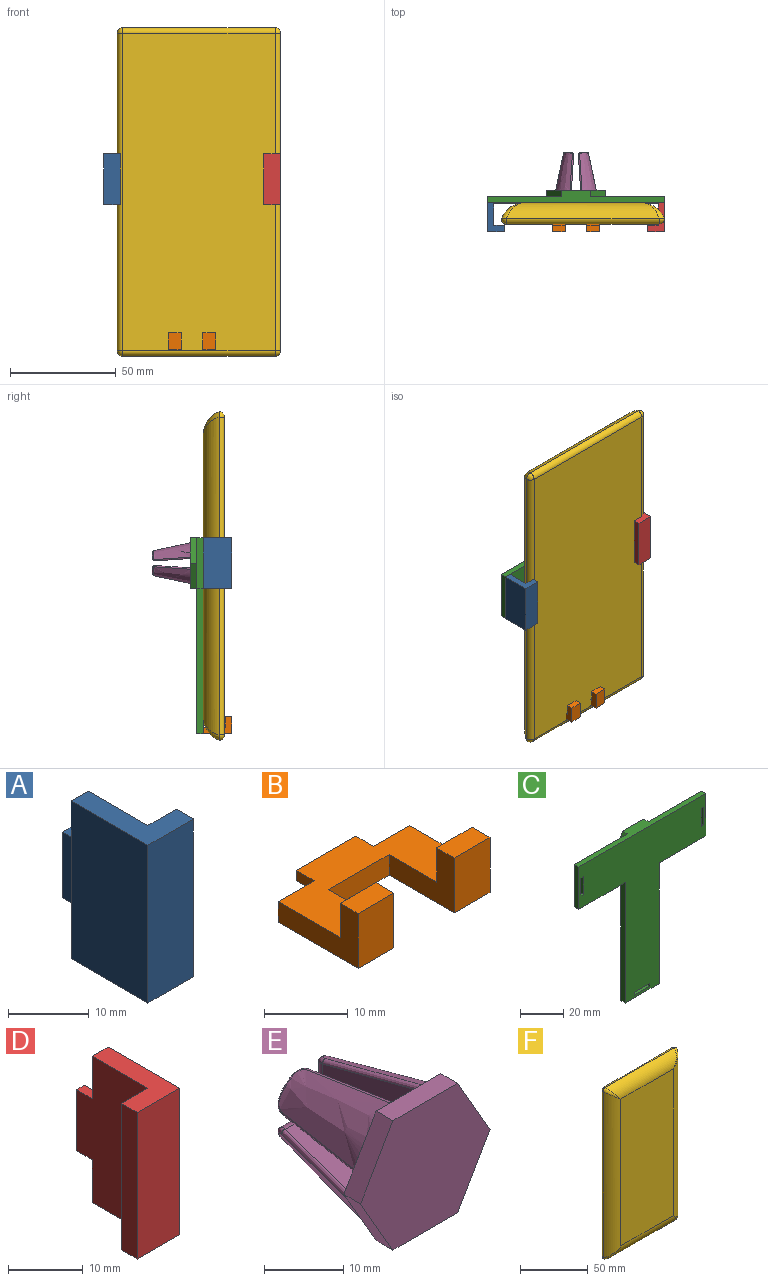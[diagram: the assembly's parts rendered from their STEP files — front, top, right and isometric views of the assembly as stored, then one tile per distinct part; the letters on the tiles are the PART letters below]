
ASSEMBLY  parts=6 mates=5
PART A: 12 faces, bbox 8x16.5x24 mm
  f0: plane 13.5x8mm, normal (0,0,-1), area 55.5mm2, adj f1,f4,f5,f6,f7,f11
  f1: plane 24x13.5mm, normal (1,0,0), area 282mm2, adj f0,f2,f3,f7,f8,f10,f11
  f2: plane 13.5x8mm, normal (0,0,1), area 55.5mm2, adj f1,f4,f5,f6,f7,f11
  f3: plane 10x1.5mm, normal (0,1,0), area 15mm2, adj f1,f8,f9,f10
  f4: plane 24x13.5mm, normal (-1,0,0), area 324mm2, adj f0,f2,f6,f11
  f5: plane 24x3mm, normal (1,0,0), area 72mm2, adj f0,f2,f6,f7
  f6: plane 24x8mm, normal (0,-1,0), area 192mm2, adj f0,f2,f4,f5
  f7: plane 24x5mm, normal (0,1,0), area 120mm2, adj f0,f1,f2,f5
  f8: plane 3x1.5mm, normal (0,0,1), area 4.5mm2, adj f1,f3,f9,f11
  f9: plane 10x3mm, normal (-1,0,0), area 30mm2, adj f3,f8,f10,f11
  f10: plane 3x1.5mm, normal (0,0,-1), area 4.5mm2, adj f1,f3,f9,f11
  f11: plane 24x3mm, normal (0,1,0), area 57mm2, adj f0,f1,f2,f4,f8,f9,f10
PART B: 18 faces, bbox 22.2x16.5x8 mm
  f0: plane 10x1.5mm, normal (0,1,0), area 15mm2, adj f1,f2,f3,f4
  f1: plane 22.2x13.5mm, normal (0,0,1), area 181.5mm2, adj f0,f3,f4,f5,f6,f7,f9,f12
  f2: plane 10x3mm, normal (0,0,-1), area 30mm2, adj f0,f3,f4,f5
  f3: plane 3x1.5mm, normal (-1,0,0), area 4.5mm2, adj f0,f1,f2,f5
  f4: plane 3x1.5mm, normal (1,0,0), area 4.5mm2, adj f0,f1,f2,f5
  f5: plane 22.2x3mm, normal (0,1,0), area 51.6mm2, adj f1,f2,f3,f4,f7,f8,f16
  f6: plane 11x8mm, normal (1,0,0), area 48mm2, adj f1,f8,f9,f10,f11,f17
  f7: plane 13.5x8mm, normal (-1,0,0), area 55.5mm2, adj f1,f5,f8,f9,f10,f11
  f8: plane 22.2x13.5mm, normal (0,0,-1), area 187.5mm2, adj f5,f6,f7,f11,f12,f15,f16,f17
  f9: plane 6x5mm, normal (0,1,0), area 30mm2, adj f1,f6,f7,f10
  f10: plane 6x3mm, normal (0,0,1), area 18mm2, adj f6,f7,f9,f11
  f11: plane 8x6mm, normal (0,-1,0), area 48mm2, adj f6,f7,f8,f10
  f12: plane 11x8mm, normal (-1,0,0), area 48mm2, adj f1,f8,f13,f14,f15,f17
  f13: plane 6x5mm, normal (0,1,0), area 30mm2, adj f1,f12,f14,f16
  f14: plane 6x3mm, normal (0,0,1), area 18mm2, adj f12,f13,f15,f16
  f15: plane 8x6mm, normal (0,-1,0), area 48mm2, adj f8,f12,f14,f16
  f16: plane 13.5x8mm, normal (1,0,0), area 55.5mm2, adj f1,f5,f8,f13,f14,f15
  f17: plane 10.2x3mm, normal (0,-1,0), area 30.6mm2, adj f1,f6,f8,f12
PART C: 35 faces, bbox 83.5x6x92.5 mm
  f0: plane 68.5x3mm, normal (-1,0,0), area 205.5mm2, adj f2,f3,f4,f5
  f1: plane 68.5x3mm, normal (1,0,0), area 205.5mm2, adj f2,f3,f4,f9
  f2: plane 22.2x3mm, normal (0,0,-1), area 66.6mm2, adj f0,f1,f3,f4
  f3: plane 92.5x83.5mm, normal (0,1,0), area 2977.4mm2, adj f0,f1,f2,f5,f6,f7,f8,f9
  f4: plane 92.5x83.5mm, normal (0,-1,0), area 3476.2mm2, adj f0,f1,f2,f5,f6,f7,f8,f9
  f5: plane 30.65x3mm, normal (0,0,-1), area 91.9mm2, adj f0,f3,f4,f8
  f6: plane 24x3mm, normal (1,0,0), area 72mm2, adj f3,f4,f7,f9
  f7: plane 83.5x6mm, normal (0,0,1), area 292.1mm2, adj f3,f4,f6,f8,f16,f17,f21
  f8: plane 24x3mm, normal (-1,0,0), area 72mm2, adj f3,f4,f5,f7
  f9: plane 30.65x3mm, normal (0,0,-1), area 91.9mm2, adj f1,f3,f4,f6
  f10: plane 10.1x5.83mm, normal (0.87,0,-0.5), area 35mm2, adj f11,f20,f21,f22
  f11: plane 10.1x5.83mm, normal (0.87,0,0.5), area 35mm2, adj f10,f12,f21,f22
  f12: plane 11.66x3mm, normal (0,0,1), area 35mm2, adj f11,f13,f21,f22
  f13: plane 10.1x5.83mm, normal (-0.87,0,0.5), area 35mm2, adj f12,f14,f21,f22
  f14: plane 10.1x5.83mm, normal (-0.87,0,-0.5), area 35mm2, adj f13,f20,f21,f22
  f15: plane 12x6.93mm, normal (-0.87,0,-0.5), area 41.6mm2, adj f3,f16,f19,f21
  f16: plane 12x6.93mm, normal (-0.87,0,0.5), area 41.6mm2, adj f3,f7,f15,f21
  f17: plane 12x6.93mm, normal (0.87,0,0.5), area 41.6mm2, adj f3,f7,f18,f21
  f18: plane 12x6.93mm, normal (0.87,0,-0.5), area 41.6mm2, adj f3,f17,f19,f21
  f19: plane 13.86x3mm, normal (0,0,-1), area 41.6mm2, adj f3,f15,f18,f21
  f20: plane 11.66x3mm, normal (0,0,-1), area 35mm2, adj f10,f14,f21,f22
  f21: plane 27.71x24mm, normal (0,1,0), area 145.5mm2, adj f7,f10,f11,f12,f13,f14,f15,f16
  f22: plane 23.33x20.2mm, normal (0,1,0), area 353.4mm2, adj f10,f11,f12,f13,f14,f20
  f23: plane 10.1x3mm, normal (1,0,0), area 30.3mm2, adj f3,f4,f24,f25
  f24: plane 3x1.6mm, normal (0,0,-1), area 4.8mm2, adj f3,f4,f23,f26
  f25: plane 3x1.6mm, normal (0,0,1), area 4.8mm2, adj f3,f4,f23,f26
  f26: plane 10.1x3mm, normal (-1,0,0), area 30.3mm2, adj f3,f4,f24,f25
  f27: plane 10.1x3mm, normal (0,0,1), area 30.3mm2, adj f3,f4,f28,f29
  f28: plane 3x1.6mm, normal (1,0,0), area 4.8mm2, adj f3,f4,f27,f30
  f29: plane 3x1.6mm, normal (-1,0,0), area 4.8mm2, adj f3,f4,f27,f30
  f30: plane 10.1x3mm, normal (0,0,-1), area 30.3mm2, adj f3,f4,f28,f29
  f31: plane 10.1x3mm, normal (1,0,0), area 30.3mm2, adj f3,f4,f32,f33
  f32: plane 3x1.6mm, normal (0,0,-1), area 4.8mm2, adj f3,f4,f31,f34
  f33: plane 3x1.6mm, normal (0,0,1), area 4.8mm2, adj f3,f4,f31,f34
  f34: plane 10.1x3mm, normal (-1,0,0), area 30.3mm2, adj f3,f4,f32,f33
PART D: 12 faces, bbox 8x16.5x24 mm
  f0: plane 13.5x8mm, normal (0,0,-1), area 55.5mm2, adj f1,f3,f5,f6,f7,f11
  f1: plane 24x13.5mm, normal (1,0,0), area 324mm2, adj f0,f4,f6,f11
  f2: plane 10x1.5mm, normal (0,1,0), area 15mm2, adj f3,f8,f9,f10
  f3: plane 24x13.5mm, normal (-1,0,0), area 282mm2, adj f0,f2,f4,f7,f8,f10,f11
  f4: plane 13.5x8mm, normal (0,0,1), area 55.5mm2, adj f1,f3,f5,f6,f7,f11
  f5: plane 24x3mm, normal (-1,0,0), area 72mm2, adj f0,f4,f6,f7
  f6: plane 24x8mm, normal (0,-1,0), area 192mm2, adj f0,f1,f4,f5
  f7: plane 24x5mm, normal (0,1,0), area 120mm2, adj f0,f3,f4,f5
  f8: plane 3x1.5mm, normal (0,0,-1), area 4.5mm2, adj f2,f3,f9,f11
  f9: plane 10x3mm, normal (1,0,0), area 30mm2, adj f2,f8,f10,f11
  f10: plane 3x1.5mm, normal (0,0,1), area 4.5mm2, adj f2,f3,f9,f11
  f11: plane 24x3mm, normal (0,1,0), area 57mm2, adj f0,f1,f3,f4,f8,f9,f10
PART E: 60 faces, bbox 23.2x23.4x20.6 mm
  f0: bspline ~17.61x8.12mm, area 143.4mm2, adj f4,f18,f19,f20,f48,f52
  f1: bspline ~17.61x8.12mm, area 143.4mm2, adj f4,f22,f23,f24,f43,f47
  f2: bspline ~17.61x8.12mm, area 143.4mm2, adj f4,f26,f27,f28,f38,f42
  f3: bspline ~17.61x8.12mm, area 143.4mm2, adj f4,f30,f31,f32,f33,f37
  f4: plane 23.15x20.06mm, normal (0,1,0), area 188.5mm2, adj f0,f1,f2,f3,f6,f7,f9,f10
  f5: plane 2.36x2.36mm, normal (0,1,0), area 3.3mm2, adj f31,f34,f36
  f6: plane 16.4x7.48mm, normal (-1,-0.07,0), area 85.4mm2, adj f4,f29,f32,f34
  f7: plane 16.4x7.48mm, normal (0,-0.07,-1), area 85.4mm2, adj f4,f29,f30,f36
  f8: plane 2.36x2.36mm, normal (0,1,0), area 3.3mm2, adj f27,f39,f41
  f9: plane 16.4x7.48mm, normal (1,-0.07,0), area 85.4mm2, adj f4,f25,f28,f39
  f10: plane 16.4x7.48mm, normal (0,-0.07,-1), area 85.4mm2, adj f4,f25,f26,f41
  f11: plane 2.36x2.36mm, normal (0,1,0), area 3.3mm2, adj f23,f44,f46
  f12: plane 16.4x7.48mm, normal (-1,-0.07,0), area 85.4mm2, adj f4,f21,f24,f44
  f13: plane 16.4x7.48mm, normal (0,-0.07,1), area 85.4mm2, adj f4,f21,f22,f46
  f14: plane 2.36x2.36mm, normal (0,1,0), area 3.3mm2, adj f19,f49,f51
  f15: plane 16.4x7.48mm, normal (0,-0.07,1), area 85.4mm2, adj f4,f17,f20,f49
  f16: plane 16.4x7.48mm, normal (1,-0.07,0), area 85.4mm2, adj f4,f17,f18,f51
  f17: cylinder r=0.5mm len=16.41mm, axis (-0.07,-1,-0.07), area 12.9mm2, adj f4,f15,f16,f50
  f18: bspline ~22.72x5.45mm, area 15.7mm2, adj f0,f4,f16,f52
  f19: bspline ~3.89x3.54mm, area 2.4mm2, adj f0,f14,f48,f52
  f20: bspline ~22.72x5.45mm, area 15.7mm2, adj f0,f4,f15,f48
  f21: cylinder r=0.5mm len=16.41mm, axis (0.07,-1,-0.07), area 12.9mm2, adj f4,f12,f13,f45
  f22: bspline ~22.72x5.45mm, area 15.7mm2, adj f1,f4,f13,f47
  f23: bspline ~3.89x3.54mm, area 2.4mm2, adj f1,f11,f43,f47
  f24: bspline ~22.72x5.45mm, area 15.7mm2, adj f1,f4,f12,f43
  f25: cylinder r=0.5mm len=16.41mm, axis (-0.07,-1,0.07), area 12.9mm2, adj f4,f9,f10,f40
  f26: bspline ~22.72x5.45mm, area 15.7mm2, adj f2,f4,f10,f42
  f27: bspline ~3.89x3.54mm, area 2.4mm2, adj f2,f8,f38,f42
  f28: bspline ~22.72x5.45mm, area 15.7mm2, adj f2,f4,f9,f38
  f29: cylinder r=0.5mm len=16.41mm, axis (-0.07,1,-0.07), area 12.9mm2, adj f4,f6,f7,f35
  f30: bspline ~20.18x4.91mm, area 15.7mm2, adj f3,f4,f7,f37
  f31: bspline ~3.62x3.43mm, area 2.4mm2, adj f3,f5,f33,f37
  f32: bspline ~20.18x4.91mm, area 15.7mm2, adj f3,f4,f6,f33
  f33: bspline ~2.03x1.75mm, area 1.9mm2, adj f3,f31,f32,f34
  f34: cylinder r=1.5mm len=4mm, axis (0,0,-1), area 7.8mm2, adj f5,f6,f33,f35
  f35: bspline ~1.76x1.5mm, area 0.9mm2, adj f29,f34,f36
  f36: cylinder r=1.5mm len=4mm, axis (-1,0,0), area 7.8mm2, adj f5,f7,f35,f37
  f37: bspline ~1.99x1.93mm, area 1.9mm2, adj f3,f30,f31,f36
  f38: bspline ~1.99x1.93mm, area 1.9mm2, adj f2,f27,f28,f39
  f39: cylinder r=1.5mm len=4mm, axis (0,0,-1), area 7.8mm2, adj f8,f9,f38,f40
  f40: bspline ~1.76x1.5mm, area 0.9mm2, adj f25,f39,f41
  f41: cylinder r=1.5mm len=4mm, axis (1,0,0), area 7.8mm2, adj f8,f10,f40,f42
  f42: bspline ~2.03x1.75mm, area 1.9mm2, adj f2,f26,f27,f41
  f43: bspline ~1.99x1.93mm, area 1.9mm2, adj f1,f23,f24,f44
  f44: cylinder r=1.5mm len=4mm, axis (0,0,1), area 7.8mm2, adj f11,f12,f43,f45
  f45: bspline ~1.76x1.5mm, area 0.9mm2, adj f21,f44,f46
  f46: cylinder r=1.5mm len=4mm, axis (-1,0,0), area 7.8mm2, adj f11,f13,f45,f47
  f47: bspline ~2.03x1.75mm, area 1.9mm2, adj f1,f22,f23,f46
  f48: bspline ~1.99x1.93mm, area 1.9mm2, adj f0,f19,f20,f49
  f49: cylinder r=1.5mm len=4mm, axis (1,0,0), area 7.8mm2, adj f14,f15,f48,f50
  f50: bspline ~1.76x1.5mm, area 0.9mm2, adj f17,f49,f51
  f51: cylinder r=1.5mm len=4mm, axis (0,0,1), area 7.8mm2, adj f14,f16,f50,f52
  f52: bspline ~2.03x1.75mm, area 1.9mm2, adj f0,f18,f19,f51
  f53: plane 11.55x3mm, normal (0,0,1), area 34.6mm2, adj f4,f54,f58,f59
  f54: plane 10x5.77mm, normal (0.87,0,0.5), area 34.6mm2, adj f4,f53,f55,f59
  f55: plane 10x5.77mm, normal (0.87,0,-0.5), area 34.6mm2, adj f4,f54,f56,f59
  f56: plane 11.55x3mm, normal (0,0,-1), area 34.6mm2, adj f4,f55,f57,f59
  f57: plane 10x5.77mm, normal (-0.87,0,-0.5), area 34.6mm2, adj f4,f56,f58,f59
  f58: plane 10x5.77mm, normal (-0.87,0,0.5), area 34.6mm2, adj f4,f53,f57,f59
  f59: plane 23.09x20mm, normal (0,-1,0), area 346.4mm2, adj f53,f54,f55,f56,f57,f58
PART F: 18 faces, bbox 77x10x155 mm
  f0: plane 132.75x54.75mm, normal (0,-1,0), area 7268.3mm2, adj f10,f13,f14,f17
  f1: plane 150x72mm, normal (0,1,0), area 10800mm2, adj f3,f4,f7,f8
  f2: sphere r=2.5mm, area 9.8mm2, adj f3,f4,f11
  f3: cylinder r=2.5mm len=72mm, axis (-1,0,0), area 282.7mm2, adj f1,f2,f5,f13
  f4: cylinder r=2.5mm len=150mm, axis (0,0,-1), area 589mm2, adj f1,f2,f6,f10
  f5: sphere r=2.5mm, area 13.4mm2, adj f3,f7,f15
  f6: sphere r=2.5mm, area 9.8mm2, adj f4,f8,f12
  f7: cylinder r=2.5mm len=150mm, axis (0,0,1), area 589mm2, adj f1,f5,f9,f17
  f8: cylinder r=2.5mm len=72mm, axis (1,0,0), area 282.7mm2, adj f1,f6,f9,f14
  f9: sphere r=2.5mm, area 6.2mm2, adj f7,f8,f16
  f10: cylinder r=12mm len=150mm, axis (0,0,-1), area 2012.7mm2, adj f0,f4,f11,f12
  f11: bspline ~11.12x11.12mm, area 22.9mm2, adj f2,f10,f13
  f12: bspline ~11.12x11.12mm, area 22.9mm2, adj f6,f10,f14
  f13: cylinder r=12mm len=72mm, axis (1,0,0), area 902.3mm2, adj f0,f3,f11,f15
  f14: cylinder r=12mm len=72mm, axis (1,0,0), area 902.3mm2, adj f0,f8,f12,f16
  f15: bspline ~11.12x11.12mm, area 23.1mm2, adj f5,f13,f17
  f16: bspline ~11.12x11.12mm, area 22.9mm2, adj f9,f14,f17
  f17: cylinder r=12mm len=150mm, axis (0,0,-1), area 2012.7mm2, adj f0,f7,f15,f16
PLACE A t=(-81.2,-40.39,27.55)mm
PLACE B t=(-94.2,-40.39,40.65)mm
PLACE C t=(-94.2,-40.39,27.55)mm
PLACE D t=(-107.2,-40.39,27.55)mm
PLACE E t=(-94.2,-57.39,27.55)mm
PLACE F rot(axis=(1,0,0),180deg) t=(-232.27,-70.39,-8.84)mm
MATE fastened B.f0 <-> C.f3  axis (0,1,0) through (-94.2,-57.39,-49.85)mm
MATE fastened E.f59 <-> C.f22  axis (0,-1,0) through (-94.2,-57.39,27.55)mm
MATE planar C.f4 <-> F.f0  axis (0,-1,0) through (-94.2,-60.39,7.69)mm
MATE fastened D.f2 <-> C.f3  axis (0,1,0) through (-53.95,-57.39,27.55)mm
MATE fastened A.f3 <-> C.f3  axis (0,1,0) through (-134.45,-57.39,27.55)mm
